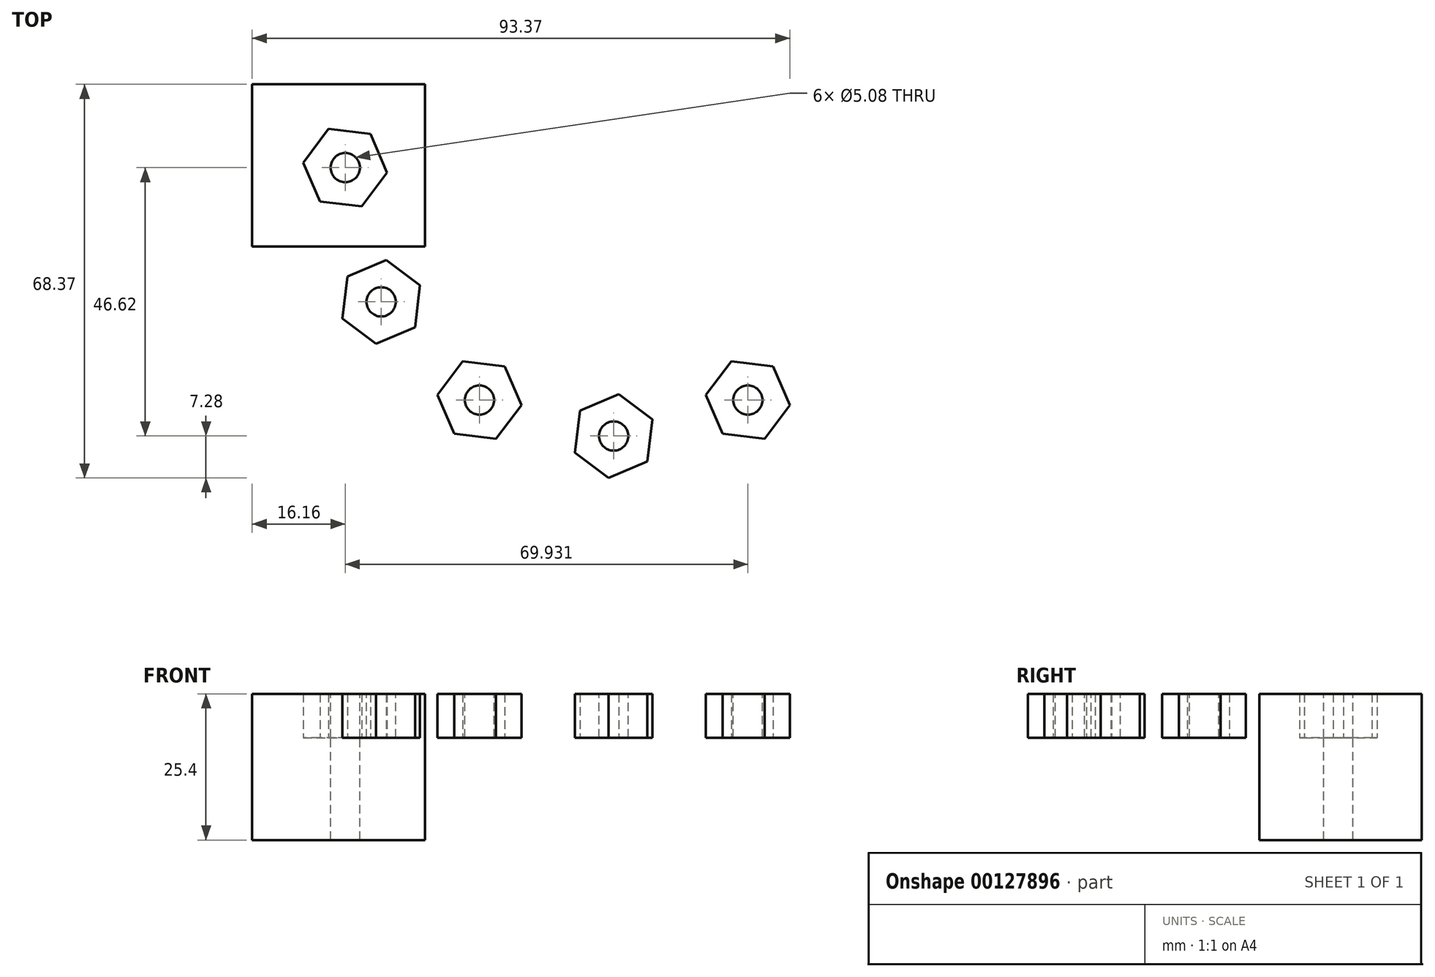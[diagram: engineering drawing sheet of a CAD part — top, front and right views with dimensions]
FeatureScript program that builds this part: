
annotation { "Feature Type Name" : "Feature", "Feature Type Description" : "" }
export const myFeature = defineFeature(function(context is Context, id is Id, definition is map)
    precondition{}
    {
        {
            var Q0;
            Q0=qCreatedBy(makeId("Top.planeOp"),FACE);
            var sketch = newSketch(context, id + "F0", { "sketchPlane" : qUnion([Q0])});
            skCircle(sketch, "E0.cCircle", {"center": v(0, 0) * mm, "radius": 6.35 * mm, "construction": true});
            skLineSegment(sketch, "E0.0", {"start": v(4.4, 5.87) * mm, "end": v(7.28, -0.87) * mm});
            skLineSegment(sketch, "E0.1", {"start": v(7.28, -0.87) * mm, "end": v(2.89, -6.74) * mm});
            skLineSegment(sketch, "E0.2", {"start": v(2.89, -6.74) * mm, "end": v(-4.4, -5.87) * mm});
            skLineSegment(sketch, "E0.3", {"start": v(-4.4, -5.87) * mm, "end": v(-7.28, 0.87) * mm});
            skLineSegment(sketch, "E0.4", {"start": v(-7.28, 0.87) * mm, "end": v(-2.89, 6.74) * mm});
            skLineSegment(sketch, "E0.5", {"start": v(-2.89, 6.74) * mm, "end": v(4.4, 5.87) * mm});
            skPoint(sketch, "E0.0.midPoint", {"position": v(5.84, 2.5) * mm});
            skSolve(sketch);
        }
        {
            var Q0;
            Q0=makeQuery(id+"F0.imprint","IMPRINT",FACE,{"disambiguationData":[TD([[makeQuery(id+"F0.imprint","IMPRINT",EDGE,{"derivedFrom":sQuery(id+"F0.wireOp",EDGE,"E0.0")}),-1.0]])]});
            extrude(context, id + "F1", {"entities" : qUnion([Q0]), "depth" : 7.62 * mm});
        }
        {
            var Q0;
            Q0=makeQuery(id+"F1.opExtrude","CAP_FACE",FACE,{"disambiguationData":[OSD([sQuery(id+"F0.wireOp",EDGE,"E0.0"),sQuery(id+"F0.wireOp",EDGE,"E0.1"),sQuery(id+"F0.wireOp",EDGE,"E0.2"),sQuery(id+"F0.wireOp",EDGE,"E0.3"),sQuery(id+"F0.wireOp",EDGE,"E0.4"),sQuery(id+"F0.wireOp",EDGE,"E0.5")])],"isStart":false});
            var sketch = newSketch(context, id + "F2", { "sketchPlane" : qUnion([Q0])});
            skCircle(sketch, "E1", {"center": v(0, 0) * mm, "radius": 2.54 * mm});
            skSolve(sketch);
        }
        {
            var Q0;
            Q0=makeQuery(id+"F2.imprint","IMPRINT",FACE,{"disambiguationData":[TD([[makeQuery(id+"F2.imprint","IMPRINT",EDGE,{"derivedFrom":sQuery(id+"F2.wireOp",EDGE,"E1")}),1.0]])]});
            extrude(context, id + "F3", {"entities" : qUnion([Q0]), "operationType" : NewBodyOperationType.REMOVE, "oppositeDirection" : true, "depth" : 25.4 * mm});
        }
        {
            var Q0;
            Q0=makeQuery(id+"F1.opExtrude","CAP_FACE",FACE,{"disambiguationData":[OSD([sQuery(id+"F0.wireOp",EDGE,"E0.0"),sQuery(id+"F0.wireOp",EDGE,"E0.1"),sQuery(id+"F0.wireOp",EDGE,"E0.2"),sQuery(id+"F0.wireOp",EDGE,"E0.3"),sQuery(id+"F0.wireOp",EDGE,"E0.4"),sQuery(id+"F0.wireOp",EDGE,"E0.5")])],"isStart":false});
            var sketch = newSketch(context, id + "F4", { "sketchPlane" : qUnion([Q0])});
            skLineSegment(sketch, "E2.bottom", {"start": v(13.84, 14.47) * mm, "end": v(-16.16, 14.47) * mm});
            skLineSegment(sketch, "E2.top", {"start": v(13.84, -13.7) * mm, "end": v(-16.16, -13.7) * mm});
            skLineSegment(sketch, "E2.left", {"start": v(13.84, 14.47) * mm, "end": v(13.84, -13.7) * mm});
            skLineSegment(sketch, "E2.right", {"start": v(-16.16, 14.47) * mm, "end": v(-16.16, -13.7) * mm});
            skSolve(sketch);
        }
        {
            var Q0;
            Q0=makeQuery(id+"F4.imprint","IMPRINT",FACE,{"disambiguationData":[TD([[makeQuery(id+"F4.imprint","IMPRINT",EDGE,{"derivedFrom":sQuery(id+"F4.wireOp",EDGE,"E2.bottom")}),1.0]])]});
            var Q1;
            Q1=makeQuery(id+"F4.imprint","IMPRINT",FACE,{"disambiguationData":[TD([[makeQuery(id+"F4.imprint","IMPRINT",EDGE,{"derivedFrom":makeQuery(id+"F1.opExtrude","CAP_EDGE",EDGE,{"disambiguationData":[OSD([sQuery(id+"F0.wireOp",EDGE,"E0.0")])],"isStart":false})}),-1.0]])]});
            var Q2;
            Q2=makeQuery(id+"F4.imprint","IMPRINT",FACE,{"disambiguationData":[TD([[makeQuery(id+"F4.imprint","IMPRINT",EDGE,{"derivedFrom":makeQuery(id+"F3.boolean.opBoolean","COPY",EDGE,{"derivedFrom":makeQuery(id+"F3.opExtrude","CAP_EDGE",EDGE,{"disambiguationData":[OSD([sQuery(id+"F2.wireOp",EDGE,"E1")])],"isStart":true})})}),1.0]])]});
            extrude(context, id + "F5", {"entities" : qUnion([Q0, Q1, Q2]), "oppositeDirection" : true, "depth" : 25.4 * mm});
        }
        {
            var Q0;
            Q0=makeQuery(id+"F1.opExtrude","SWEPT_BODY",BODY,{"disambiguationData":[OSD([sQuery(id+"F0.wireOp",EDGE,"E0.0"),sQuery(id+"F0.wireOp",EDGE,"E0.1"),sQuery(id+"F0.wireOp",EDGE,"E0.2"),sQuery(id+"F0.wireOp",EDGE,"E0.3"),sQuery(id+"F0.wireOp",EDGE,"E0.4"),sQuery(id+"F0.wireOp",EDGE,"E0.5")])]});
            var Q1;
            Q1=makeQuery(id+"F5.opExtrude","SWEPT_BODY",BODY,{"disambiguationData":[OSD([sQuery(id+"F4.wireOp",EDGE,"E2.bottom"),sQuery(id+"F4.wireOp",EDGE,"E2.top"),sQuery(id+"F4.wireOp",EDGE,"E2.left"),sQuery(id+"F4.wireOp",EDGE,"E2.right")])]});
            booleanBodies(context, id + "F6", {"operationType" : BooleanOperationType.SUBTRACTION, "tools" : qUnion([Q0]), "targets" : qUnion([Q1]), "keepTools" : true});
        }
        {
            var Q0;
            Q0=qCreatedBy(makeId("Front.planeOp"),FACE);
            var sketch = newSketch(context, id + "F7", { "sketchPlane" : qUnion([Q0])});
            skLineSegment(sketch, "E3", {"start": v(46.62, -10.8) * mm, "end": v(46.62, 31.77) * mm});
            skSolve(sketch);
        }
        {
            var Q0;
            Q0=makeQuery(id+"F1.opExtrude","SWEPT_BODY",BODY,{"disambiguationData":[OSD([sQuery(id+"F0.wireOp",EDGE,"E0.0"),sQuery(id+"F0.wireOp",EDGE,"E0.1"),sQuery(id+"F0.wireOp",EDGE,"E0.2"),sQuery(id+"F0.wireOp",EDGE,"E0.3"),sQuery(id+"F0.wireOp",EDGE,"E0.4"),sQuery(id+"F0.wireOp",EDGE,"E0.5")])]});
            var Q1;
            Q1=sQuery(id+"F7.wireOp",EDGE,"E3");
            circularPattern(context, id + "F8", {"entities" : qUnion([Q0]), "axis" : qUnion([Q1]), "angle" : 30 * degree, "instanceCount" : 5});
        }
    });
